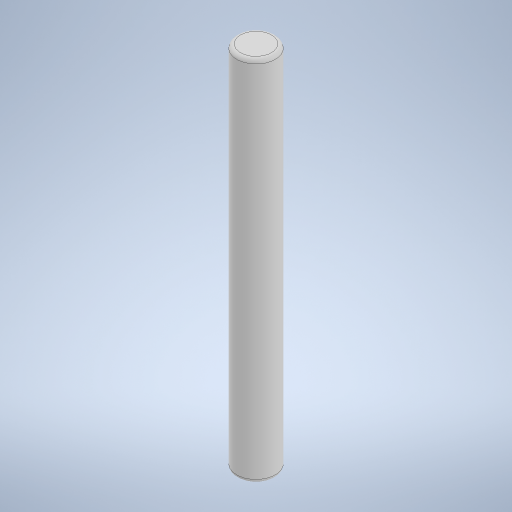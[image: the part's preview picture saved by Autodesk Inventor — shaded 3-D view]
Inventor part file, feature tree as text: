
AUTODESK INVENTOR PART (.ipt)
format: ipt  version: 2023.2 (Build 272271000, 271)  size: 233,984 bytes
history: native  units: in
note: dims shown in document units (in); Inventor stores cm internally (conversion verified against a paired STEP export)
features: extrude x1, fillet x1, sketch x1
ambient origin geometry x8: Origin, YZ Plane, XZ Plane, XY Plane, X Axis, Y Axis, Z Axis, Center Point
bodies: Solid1 (feature_tree)
feature tree (3):
  extrude  "Extrusion1"  Depth=1.8701in TaperAngle=0.0deg
  fillet  "Fillet1"  Radius=0.0197in
  sketch  "Sketch1"  dims[d0=0.1969in d1=1.8701in d2=0.0in d3=0.0197in]
